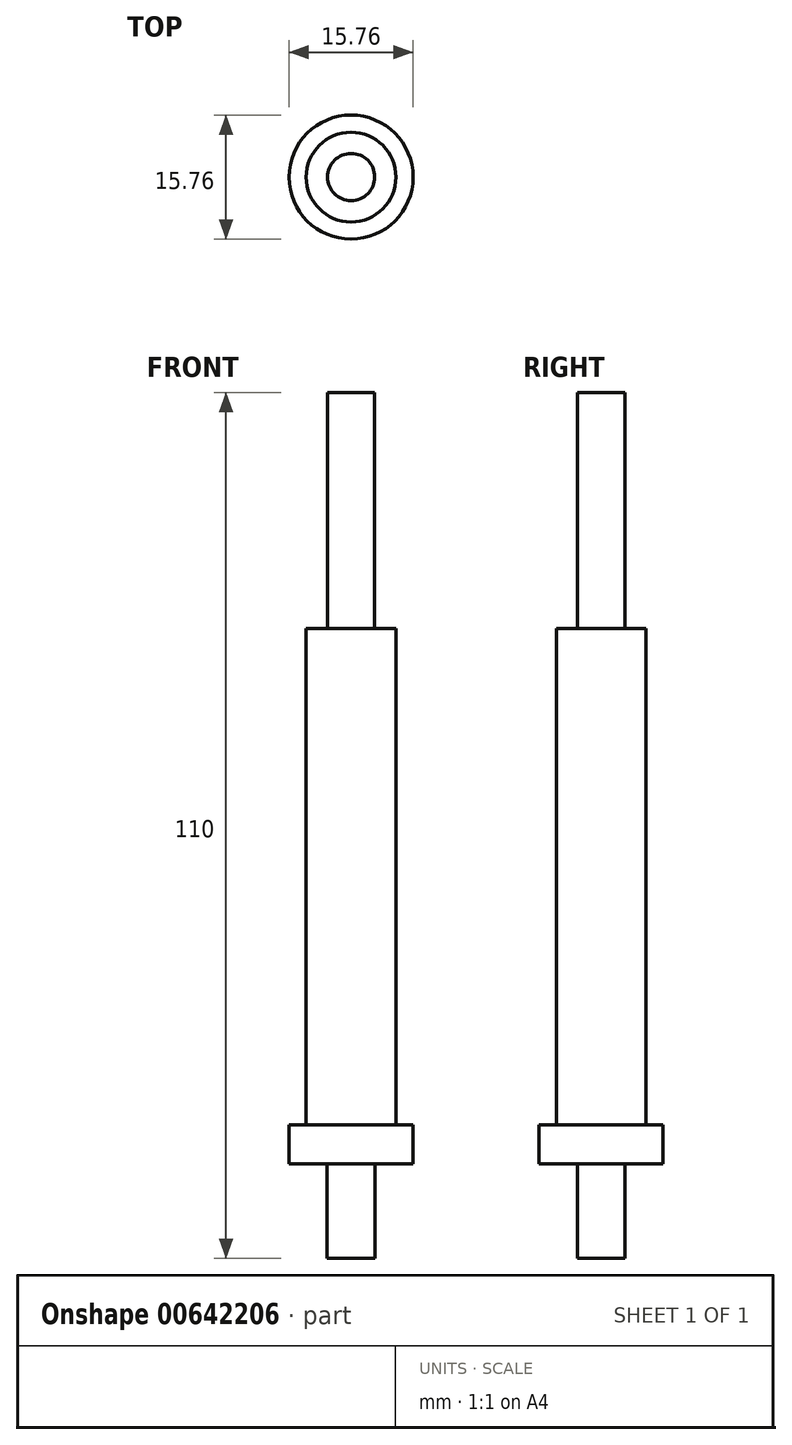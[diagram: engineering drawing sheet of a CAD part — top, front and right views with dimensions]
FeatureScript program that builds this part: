
annotation { "Feature Type Name" : "Feature", "Feature Type Description" : "" }
export const myFeature = defineFeature(function(context is Context, id is Id, definition is map)
    precondition{}
    {
        {
            var Q0;
            Q0=qCreatedBy(makeId("Top.planeOp"),FACE);
            var sketch = newSketch(context, id + "F0", { "sketchPlane" : qUnion([Q0])});
            skCircle(sketch, "E0", {"center": v(0, 0) * mm, "radius": 5.7 * mm});
            skSolve(sketch);
        }
        {
            var Q0;
            Q0=qSketchRegion(id+"F0",true);
            extrude(context, id + "F1", {"entities" : qUnion([Q0]), "depth" : 63 * mm, "offsetDistance" : 25 * mm});
        }
        {
            var Q0;
            Q0=makeQuery(id+"F1.opExtrude","CAP_FACE",FACE,{"disambiguationData":[OSD([sQuery(id+"F0.wireOp",EDGE,"E0")])],"isStart":false});
            var sketch = newSketch(context, id + "F2", { "sketchPlane" : qUnion([Q0])});
            skCircle(sketch, "E1", {"center": v(0, 0) * mm, "radius": 3 * mm});
            skSolve(sketch);
        }
        {
            var Q0;
            Q0=qSketchRegion(id+"F2",true);
            extrude(context, id + "F3", {"entities" : qUnion([Q0]), "operationType" : NewBodyOperationType.ADD, "depth" : 30 * mm, "offsetDistance" : 25 * mm});
        }
        {
            var Q0;
            Q0=makeQuery(id+"F1.opExtrude","CAP_FACE",FACE,{"disambiguationData":[OSD([sQuery(id+"F0.wireOp",EDGE,"E0")])],"isStart":true});
            var sketch = newSketch(context, id + "F4", { "sketchPlane" : qUnion([Q0])});
            skCircle(sketch, "E2", {"center": v(0, 0) * mm, "radius": 7.88 * mm});
            skSolve(sketch);
        }
        {
            var Q0;
            Q0=qSketchRegion(id+"F4",true);
            extrude(context, id + "F5", {"entities" : qUnion([Q0]), "depth" : 5 * mm, "offsetDistance" : 25 * mm});
        }
        {
            var Q0;
            Q0=makeQuery(id+"F5.opExtrude","CAP_FACE",FACE,{"disambiguationData":[OSD([sQuery(id+"F4.wireOp",EDGE,"E2")])],"isStart":false});
            var sketch = newSketch(context, id + "F6", { "sketchPlane" : qUnion([Q0])});
            skCircle(sketch, "E3", {"center": v(0, 0) * mm, "radius": 3.03 * mm});
            skSolve(sketch);
        }
        {
            var Q0;
            Q0=qSketchRegion(id+"F6",true);
            extrude(context, id + "F7", {"entities" : qUnion([Q0]), "operationType" : NewBodyOperationType.ADD, "depth" : 12 * mm, "offsetDistance" : 25 * mm});
        }
    });
